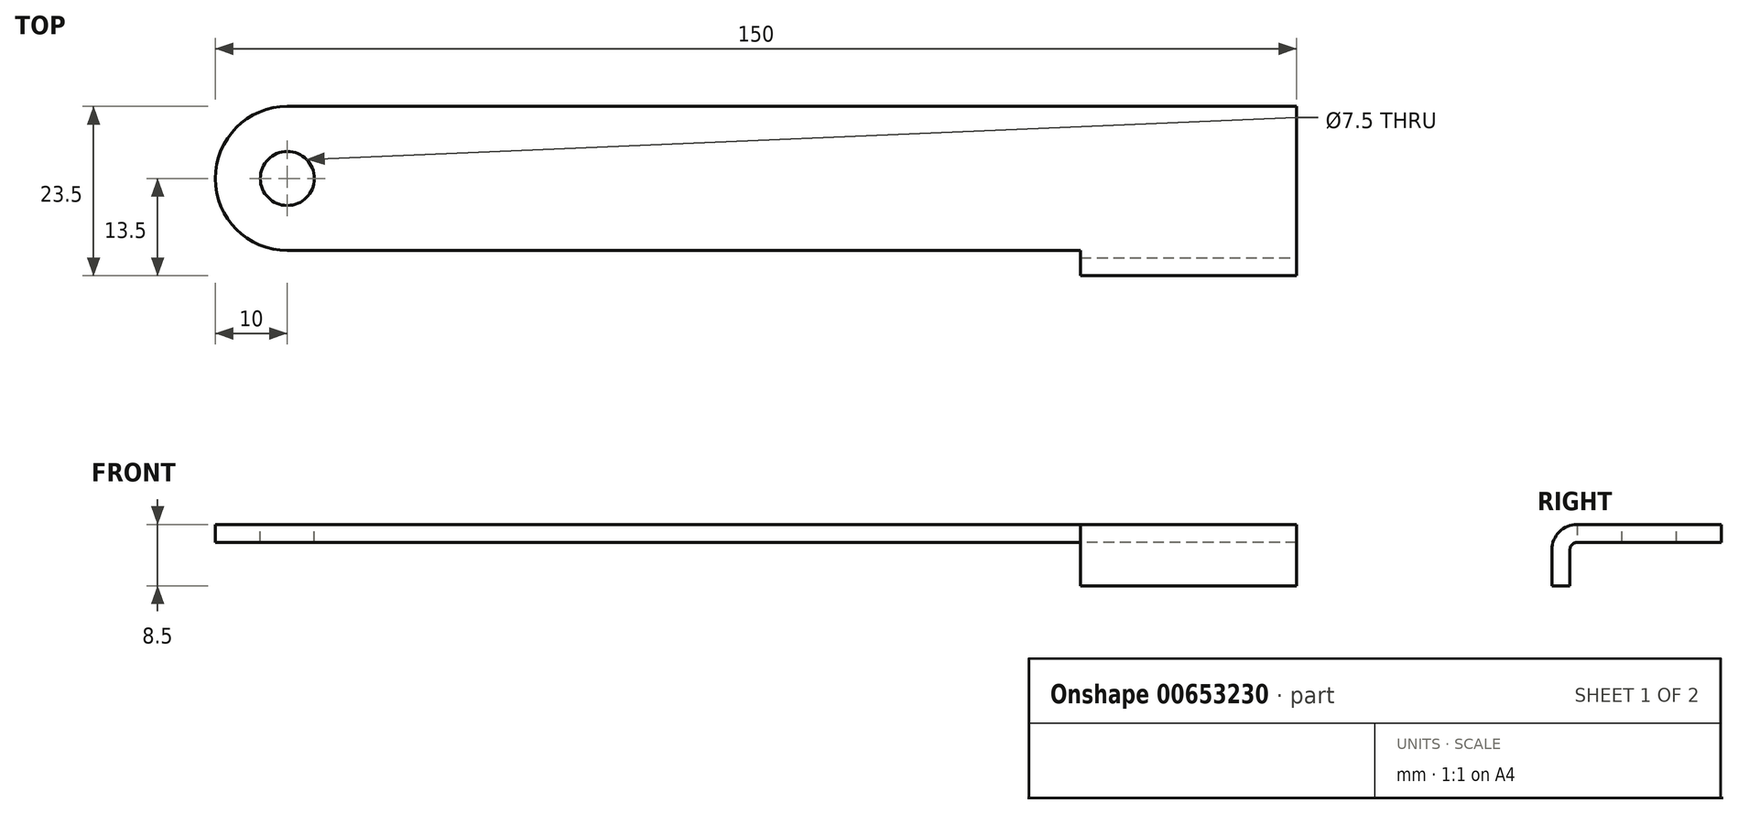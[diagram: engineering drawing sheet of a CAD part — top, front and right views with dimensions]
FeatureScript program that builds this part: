
annotation { "Feature Type Name" : "Feature", "Feature Type Description" : "" }
export const myFeature = defineFeature(function(context is Context, id is Id, definition is map)
    precondition{}
    {
        {
            var Q0;
            Q0=qCreatedBy(makeId("Top.planeOp"),FACE);
            var sketch = newSketch(context, id + "F0", { "sketchPlane" : qUnion([Q0])});
            skLineSegment(sketch, "E0.bottom", {"start": v(75, 10) * mm, "end": v(-75, 10) * mm});
            skLineSegment(sketch, "E0.top", {"start": v(75, -10) * mm, "end": v(-75, -10) * mm});
            skLineSegment(sketch, "E0.left", {"start": v(75, 10) * mm, "end": v(75, -10) * mm});
            skLineSegment(sketch, "E0.right", {"start": v(-75, 10) * mm, "end": v(-75, -10) * mm});
            skPoint(sketch, "E0.middle", {"position": v(0, 0) * mm});
            skSolve(sketch);
        }
        {
            var Q0;
            Q0 = qSketchRegion(id + "F0", true);
            extrude(context, id + "F1", {"entities" : qUnion([Q0]), "depth" : 2.5 * mm, "offsetDistance" : 25 * mm});
        }
        {
            var Q0;
            Q0=makeQuery(id+"F1.opExtrude","CAP_FACE",FACE,{"disambiguationData":[OSD([sQuery(id+"F0.wireOp",EDGE,"E0.bottom"),sQuery(id+"F0.wireOp",EDGE,"E0.top"),sQuery(id+"F0.wireOp",EDGE,"E0.left"),sQuery(id+"F0.wireOp",EDGE,"E0.right")])],"isStart":false});
            var sketch = newSketch(context, id + "F2", { "sketchPlane" : qUnion([Q0])});
            skPoint(sketch, "E1", {"position": v(-65, 0) * mm});
            skPoint(sketch, "E1.positionSnap0", {"position": v(-75, 0) * mm});
            skSolve(sketch);
        }
        {
            var Q0;
            Q0=sQuery(id+"F2.wireOp",VERTEX,"E1");
            var Q1;
            Q1=makeQuery(id+"F1.opExtrude","SWEPT_BODY",BODY,{"disambiguationData":[OSD([sQuery(id+"F0.wireOp",EDGE,"E0.bottom"),sQuery(id+"F0.wireOp",EDGE,"E0.top"),sQuery(id+"F0.wireOp",EDGE,"E0.left"),sQuery(id+"F0.wireOp",EDGE,"E0.right")])]});
            hole(context, id + "F3", {"style" : HoleStyle.SIMPLE, "endStyle" : HoleEndStyle.THROUGH, "holeDiameter" : 7.5 * mm, "majorDiameter" : 4 * mm, "isTappedThrough" : true, "tappedDepth" : 12 * mm, "tapClearance" : 3, "startFromSketch" : true, "locations" : qUnion([Q0]), "scope" : qUnion([Q1])});
        }
        {
            var Q0;
            Q0=makeQuery(id+"F1.opExtrude","SWEPT_EDGE",EDGE,{"disambiguationData":[OSD([sQuery(id+"F0.wireOp",EDGE,"E0.top"),sQuery(id+"F0.wireOp",EDGE,"E0.right")])]});
            var Q1;
            Q1=makeQuery(id+"F1.opExtrude","SWEPT_EDGE",EDGE,{"disambiguationData":[OSD([sQuery(id+"F0.wireOp",EDGE,"E0.bottom"),sQuery(id+"F0.wireOp",EDGE,"E0.right")])]});
            fillet(context, id + "F4", {"entities" : qUnion([Q0, Q1]), "radius" : 10 * mm, "tangentPropagation" : true, "allowEdgeOverflow" : false});
        }
        {
            var Q0;
            Q0=makeQuery(id+"F1.opExtrude","SWEPT_FACE",FACE,{"disambiguationData":[OSD([sQuery(id+"F0.wireOp",EDGE,"E0.left")])]});
            var sketch = newSketch(context, id + "F5", { "sketchPlane" : qUnion([Q0])});
            skLineSegment(sketch, "E2.0", {"start": v(-10, 2.5) * mm, "end": v(-10, 0) * mm});
            skLineSegment(sketch, "E3.0", {"start": v(10, 2.5) * mm, "end": v(-10, 2.5) * mm, "construction": true});
            skLineSegment(sketch, "E4.0", {"start": v(10, 0) * mm, "end": v(-10, 0) * mm, "construction": true});
            skLineSegment(sketch, "E5.bottom", {"start": v(-13.5, -1) * mm, "end": v(-11, -1) * mm});
            skLineSegment(sketch, "E5.top", {"start": v(-13.5, -6) * mm, "end": v(-11, -6) * mm});
            skLineSegment(sketch, "E5.left", {"start": v(-13.5, -1) * mm, "end": v(-13.5, -6) * mm});
            skLineSegment(sketch, "E5.right", {"start": v(-11, -1) * mm, "end": v(-11, -6) * mm});
            skArc(sketch, "E6", {"start": v(-10, 0) * mm, "mid": v(-10.7, -0.3) * mm, "end": v(-11, -1) * mm});
            skArc(sketch, "E7", {"start": v(-10, 2.5) * mm, "mid": v(-12.47, 1.47) * mm, "end": v(-13.5, -1) * mm});
            skSolve(sketch);
        }
        {
            var Q0;
            Q0=makeQuery(id+"F5.imprint","IMPRINT",FACE,{"disambiguationData":[TD([[makeQuery(id+"F5.imprint","IMPRINT",EDGE,{"derivedFrom":sQuery(id+"F5.wireOp",EDGE,"E2.0")}),-1.0]])]});
            var Q1;
            Q1=makeQuery(id+"F5.imprint","IMPRINT",FACE,{"disambiguationData":[TD([[makeQuery(id+"F5.imprint","IMPRINT",EDGE,{"derivedFrom":sQuery(id+"F5.wireOp",EDGE,"E5.bottom")}),-1.0]])]});
            extrude(context, id + "F6", {"entities" : qUnion([Q0, Q1]), "operationType" : NewBodyOperationType.ADD, "oppositeDirection" : true, "depth" : 30 * mm, "offsetDistance" : 25 * mm});
        }
    });
